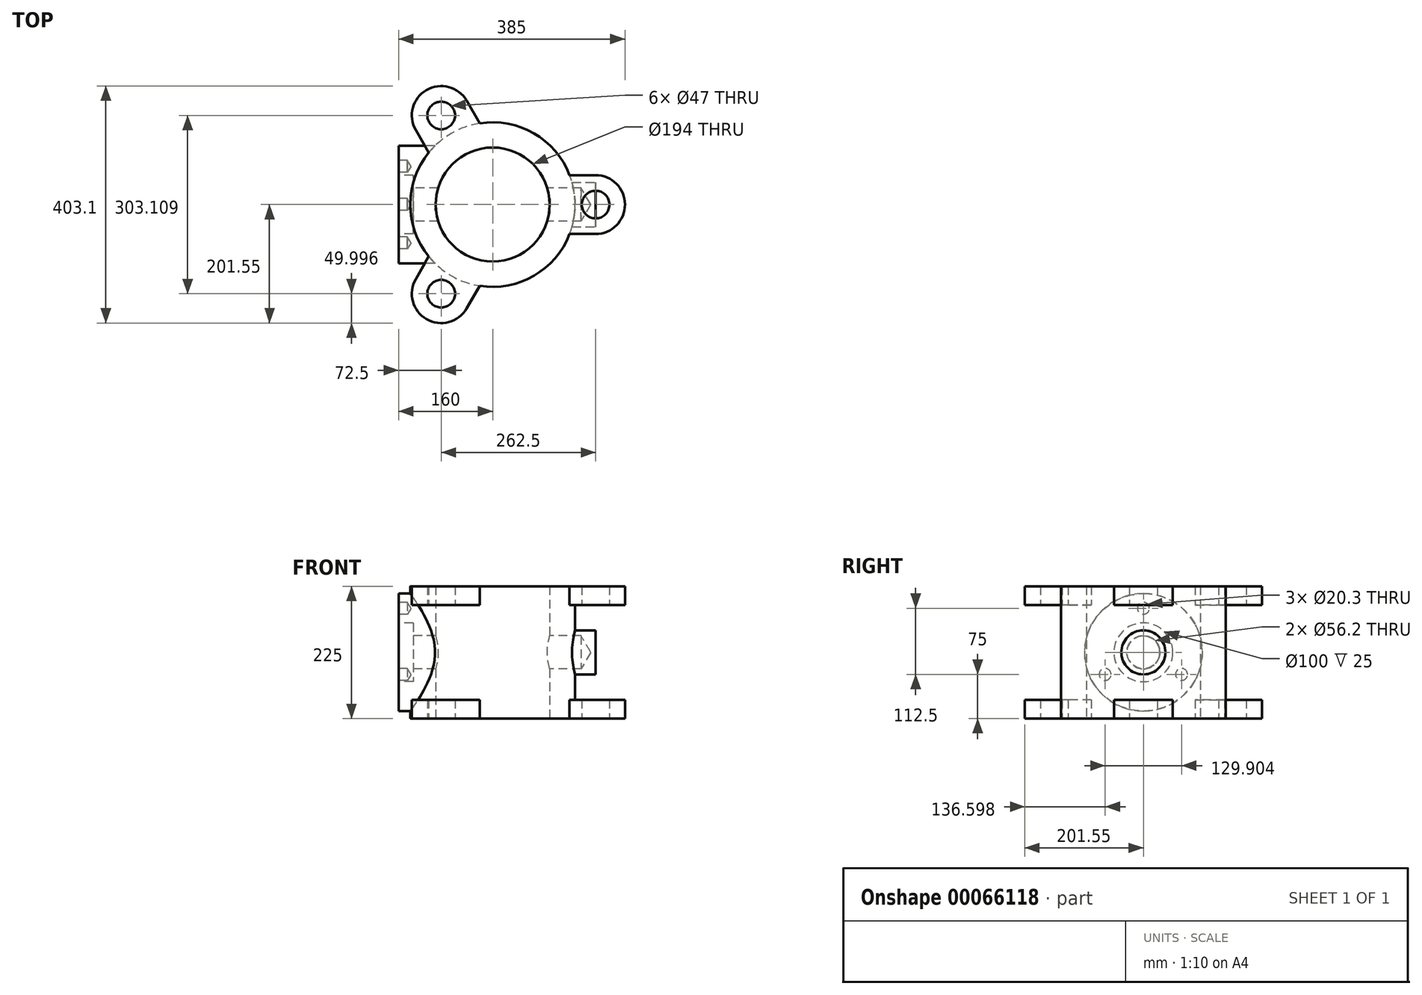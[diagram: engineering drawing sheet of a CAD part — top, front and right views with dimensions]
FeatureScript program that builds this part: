
annotation { "Feature Type Name" : "Feature", "Feature Type Description" : "" }
export const myFeature = defineFeature(function(context is Context, id is Id, definition is map)
    precondition{}
    {
        {
            var Q0;
            Q0=qCreatedBy(makeId("Top.planeOp"),FACE);
            var sketch = newSketch(context, id + "F0", { "sketchPlane" : qUnion([Q0])});
            skArc(sketch, "E0", {"start": v(130.77, 50) * mm, "mid": v(-140, 0) * mm, "end": v(130.77, -50) * mm});
            skCircle(sketch, "E1", {"center": v(0, 0) * mm, "radius": 97 * mm});
            skArc(sketch, "E2", {"start": v(175, -50) * mm, "mid": v(225, 0) * mm, "end": v(175, 50) * mm});
            skCircle(sketch, "E3", {"center": v(175, 0) * mm, "radius": 23.5 * mm});
            skLineSegment(sketch, "E4", {"start": v(130.77, 50) * mm, "end": v(175, 50) * mm});
            skLineSegment(sketch, "E5", {"start": v(130.77, -50) * mm, "end": v(175, -50) * mm});
            skSolve(sketch);
        }
        {
            var Q0;
            Q0=makeQuery(id+"F0.imprint","IMPRINT",FACE,{"disambiguationData":[TD([[makeQuery(id+"F0.imprint","IMPRINT",EDGE,{"derivedFrom":sQuery(id+"F0.wireOp",EDGE,"E0")}),1.0]])]});
            extrude(context, id + "F1", {"entities" : qUnion([Q0]), "depth" : 32 * mm});
        }
        {
            var Q0;
            Q0=makeQuery(id+"F1.opExtrude","SWEPT_BODY",BODY,{"disambiguationData":[OSD([sQuery(id+"F0.wireOp",EDGE,"E0"),sQuery(id+"F0.wireOp",EDGE,"E1"),sQuery(id+"F0.wireOp",EDGE,"E2"),sQuery(id+"F0.wireOp",EDGE,"E3"),sQuery(id+"F0.wireOp",EDGE,"E4"),sQuery(id+"F0.wireOp",EDGE,"E5")])]});
            var Q1;
            Q1=makeQuery(id+"F1.opExtrude","CAP_EDGE",EDGE,{"disambiguationData":[OSD([sQuery(id+"F0.wireOp",EDGE,"E1")])],"isStart":false});
            circularPattern(context, id + "F2", {"operationType" : NewBodyOperationType.ADD, "entities" : qUnion([Q0]), "axis" : qUnion([Q1]), "angle" : 120 * degree, "instanceCount" : 3});
        }
        {
            var Q0;
            {var subQ0=makeQuery(id+"F1.opExtrude","CAP_FACE",FACE,{"disambiguationData":[OSD([sQuery(id+"F0.wireOp",EDGE,"E0"),sQuery(id+"F0.wireOp",EDGE,"E1"),sQuery(id+"F0.wireOp",EDGE,"E2"),sQuery(id+"F0.wireOp",EDGE,"E3"),sQuery(id+"F0.wireOp",EDGE,"E4"),sQuery(id+"F0.wireOp",EDGE,"E5")])],"isStart":false});Q0=makeQuery(id+"F2.boolean.opBoolean","MERGE",FACE,{"derivedFrom":[subQ0,makeQuery(id+"F2.opPattern","COPY",FACE,{"derivedFrom":subQ0,"instanceName":"1"}),makeQuery(id+"F2.opPattern","COPY",FACE,{"derivedFrom":subQ0,"instanceName":"2"})]});}
            var sketch = newSketch(context, id + "F3", { "sketchPlane" : qUnion([Q0])});
            skCircle(sketch, "E6.0", {"center": v(0, 0) * mm, "radius": 97 * mm});
            skCircle(sketch, "E7", {"center": v(0, 0) * mm, "radius": 140 * mm});
            skSolve(sketch);
        }
        {
            var Q0;
            Q0=makeQuery(id+"F3.imprint","IMPRINT",FACE,{"disambiguationData":[TD([[makeQuery(id+"F3.imprint","IMPRINT",EDGE,{"derivedFrom":sQuery(id+"F3.wireOp",EDGE,"E6.0")}),-1.0]])]});
            extrude(context, id + "F4", {"entities" : qUnion([Q0]), "operationType" : NewBodyOperationType.ADD, "depth" : (225 - 64) * mm});
        }
        {
            var Q0;
            Q0=makeQuery(id+"F4.opExtrude","CAP_FACE",FACE,{"disambiguationData":[OSD([sQuery(id+"F3.wireOp",EDGE,"E6.0"),sQuery(id+"F3.wireOp",EDGE,"E7")])],"isStart":false});
            var sketch = newSketch(context, id + "F5", { "sketchPlane" : qUnion([Q0])});
            skLineSegment(sketch, "E8.0.0", {"start": v(175, -50) * mm, "end": v(130.77, -50) * mm});
            skArc(sketch, "E8.0.1", {"start": v(130.77, -50) * mm, "mid": v(70, -121.24) * mm, "end": v(-22.08, -138.25) * mm});
            skLineSegment(sketch, "E8.0.2", {"start": v(-22.08, -138.25) * mm, "end": v(-44.2, -176.55) * mm});
            skArc(sketch, "E8.0.3", {"start": v(-44.2, -176.55) * mm, "mid": v(-112.5, -194.86) * mm, "end": v(-130.8, -126.55) * mm});
            skLineSegment(sketch, "E8.0.4", {"start": v(-130.8, -126.55) * mm, "end": v(-108.68, -88.25) * mm});
            skArc(sketch, "E8.0.5", {"start": v(-108.68, -88.25) * mm, "mid": v(-140, 0) * mm, "end": v(-108.68, 88.25) * mm});
            skLineSegment(sketch, "E8.0.6", {"start": v(-108.68, 88.25) * mm, "end": v(-130.8, 126.55) * mm});
            skArc(sketch, "E8.0.7", {"start": v(-130.8, 126.55) * mm, "mid": v(-112.5, 194.86) * mm, "end": v(-44.2, 176.55) * mm});
            skLineSegment(sketch, "E8.0.8", {"start": v(-44.2, 176.55) * mm, "end": v(-22.08, 138.25) * mm});
            skArc(sketch, "E8.0.9", {"start": v(-22.08, 138.25) * mm, "mid": v(70, 121.24) * mm, "end": v(130.77, 50) * mm});
            skLineSegment(sketch, "E8.0.10", {"start": v(130.77, 50) * mm, "end": v(175, 50) * mm});
            skArc(sketch, "E8.0.11", {"start": v(175, 50) * mm, "mid": v(225, 0) * mm, "end": v(175, -50) * mm});
            skCircle(sketch, "E9.0", {"center": v(-87.5, -151.55) * mm, "radius": 23.5 * mm});
            skCircle(sketch, "E10.0", {"center": v(175, 0) * mm, "radius": 23.5 * mm});
            skCircle(sketch, "E11.0", {"center": v(-87.5, 151.55) * mm, "radius": 23.5 * mm});
            skCircle(sketch, "E12.0", {"center": v(0, 0) * mm, "radius": 97 * mm});
            skSolve(sketch);
        }
        {
            var Q0;
            Q0 = qSketchRegion(id + "F5", true);
            extrude(context, id + "F6", {"entities" : qUnion([Q0]), "operationType" : NewBodyOperationType.ADD, "depth" : 32 * mm});
        }
        {
            var Q0;
            Q0=qCreatedBy(makeId("Right.planeOp"),FACE);
            cPlane(context, id + "F7", {"entities" : qUnion([Q0]), "cplaneType" : CPlaneType.OFFSET, "offset" : 160 * mm, "oppositeDirection" : true, "width" : 150 * mm, "height" : 150 * mm});
        }
        {
            var Q0;
            Q0=qCreatedBy(id+"F7.planeOp",FACE);
            var sketch = newSketch(context, id + "F8", { "sketchPlane" : qUnion([Q0])});
            skCircle(sketch, "E13", {"center": v(0, 112.5) * mm, "radius": 100 * mm});
            skSolve(sketch);
        }
        {
            var Q0;
            Q0=makeQuery(id+"F8.imprint","IMPRINT",FACE,{"disambiguationData":[TD([[makeQuery(id+"F8.imprint","IMPRINT",EDGE,{"derivedFrom":sQuery(id+"F8.wireOp",EDGE,"E13")}),1.0]])]});
            extrude(context, id + "F9", {"entities" : qUnion([Q0]), "operationType" : NewBodyOperationType.ADD, "endBound" : BoundingType.UP_TO_NEXT, "depth" : 25 * mm});
        }
        {
            var Q0;
            Q0=makeQuery(id+"F9.opExtrude","CAP_FACE",FACE,{"disambiguationData":[OSD([sQuery(id+"F8.wireOp",EDGE,"E13")])],"isStart":true});
            var sketch = newSketch(context, id + "F10", { "sketchPlane" : qUnion([Q0])});
            skPoint(sketch, "E14", {"position": v(0, 112.5) * mm});
            skSolve(sketch);
        }
        {
            var Q0;
            Q0=makeQuery(id+"F9.opExtrude","CAP_FACE",FACE,{"disambiguationData":[OSD([sQuery(id+"F8.wireOp",EDGE,"E13")])],"isStart":true});
            var sketch = newSketch(context, id + "F11", { "sketchPlane" : qUnion([Q0])});
            skPoint(sketch, "E15", {"position": v(0, 187.5) * mm});
            skCircle(sketch, "E16", {"center": v(0, 112.5) * mm, "radius": 75 * mm, "construction": true});
            skPoint(sketch, "E17.1.0", {"position": v(-64.95, 75) * mm});
            skPoint(sketch, "E17.2.0", {"position": v(64.95, 75) * mm});
            skSolve(sketch);
        }
        {
            var Q0;
            Q0=sQuery(id+"F11.wireOp",VERTEX,"E15");
            var Q1;
            Q1=sQuery(id+"F11.wireOp",VERTEX,"E17.1.0");
            var Q2;
            Q2=sQuery(id+"F11.wireOp",VERTEX,"E17.2.0");
            var Q3;
            Q3=makeQuery(id+"F1.opExtrude","SWEPT_BODY",BODY,{"disambiguationData":[OSD([sQuery(id+"F0.wireOp",EDGE,"E0"),sQuery(id+"F0.wireOp",EDGE,"E1"),sQuery(id+"F0.wireOp",EDGE,"E2"),sQuery(id+"F0.wireOp",EDGE,"E3"),sQuery(id+"F0.wireOp",EDGE,"E4"),sQuery(id+"F0.wireOp",EDGE,"E5")])]});
            hole(context, id + "F12", {"style" : HoleStyle.SIMPLE, "holeDiameter" : 20.3 * mm, "endStyle" : HoleEndStyle.BLIND, "holeDepth" : 15 * mm, "locations" : qUnion([Q0, Q1, Q2]), "scope" : qUnion([Q3])});
        }
        {
            var Q0;
            Q0=qCreatedBy(makeId("Right.planeOp"),FACE);
            cPlane(context, id + "F13", {"entities" : qUnion([Q0]), "cplaneType" : CPlaneType.OFFSET, "offset" : 175 * mm, "width" : 150 * mm, "height" : 150 * mm});
        }
        {
            var Q0;
            Q0=qCreatedBy(id+"F13.planeOp",FACE);
            var sketch = newSketch(context, id + "F14", { "sketchPlane" : qUnion([Q0])});
            skCircle(sketch, "E18", {"center": v(0, 112.5) * mm, "radius": 37.5 * mm});
            skSolve(sketch);
        }
        {
            var Q0;
            Q0 = qSketchRegion(id + "F14", true);
            var Q1;
            {var subQ0=sQuery(id+"F0.wireOp",EDGE,"E5");var subQ1=sQuery(id+"F0.wireOp",EDGE,"E4");var subQ5=sQuery(id+"F0.wireOp",EDGE,"E0");var subQ11=makeQuery(id+"F1.opExtrude","SWEPT_FACE",FACE,{"disambiguationData":[OSD([subQ1])]});var subQ13=makeQuery(id+"F1.opExtrude","SWEPT_FACE",FACE,{"disambiguationData":[OSD([subQ0])]});var subQ14=makeQuery(id+"F1.opExtrude","SWEPT_FACE",FACE,{"disambiguationData":[OSD([subQ5])]});Q1=makeQuery(id+"F6.boolean.opBoolean","MERGE",FACE,{"derivedFrom":[makeQuery(id+"F4.boolean.opBoolean","MERGE",FACE,{"derivedFrom":[makeQuery(id+"F2.boolean.opBoolean","SPLIT",FACE,{"disambiguationData":[TD([subQ11])],"derivedFrom":subQ14}),makeQuery(id+"F2.boolean.opBoolean","SPLIT",FACE,{"disambiguationData":[TD([subQ13])],"derivedFrom":subQ14}),makeQuery(id+"F2.boolean.opBoolean","SPLIT",FACE,{"disambiguationData":[TD([makeQuery(id+"F2.opPattern","COPY",FACE,{"derivedFrom":subQ11,"instanceName":"1"})])],"derivedFrom":subQ14}),makeQuery(id+"F4.opExtrude","SWEPT_FACE",FACE,{"disambiguationData":[OSD([sQuery(id+"F3.wireOp",EDGE,"E7")])]})]}),makeQuery(id+"F6.opExtrude","SWEPT_FACE",FACE,{"disambiguationData":[OSD([sQuery(id+"F5.wireOp",EDGE,"E8.0.1")])]}),makeQuery(id+"F6.opExtrude","SWEPT_FACE",FACE,{"disambiguationData":[OSD([sQuery(id+"F5.wireOp",EDGE,"E8.0.5")])]}),makeQuery(id+"F6.opExtrude","SWEPT_FACE",FACE,{"disambiguationData":[OSD([sQuery(id+"F5.wireOp",EDGE,"E8.0.9")])]})]});}
            var Q2;
            Q2=makeQuery(id+"F1.opExtrude","SWEPT_BODY",BODY,{"disambiguationData":[OSD([sQuery(id+"F0.wireOp",EDGE,"E0"),sQuery(id+"F0.wireOp",EDGE,"E1"),sQuery(id+"F0.wireOp",EDGE,"E2"),sQuery(id+"F0.wireOp",EDGE,"E3"),sQuery(id+"F0.wireOp",EDGE,"E4"),sQuery(id+"F0.wireOp",EDGE,"E5")])]});
            extrude(context, id + "F15", {"entities" : qUnion([Q0]), "operationType" : NewBodyOperationType.ADD, "endBound" : BoundingType.UP_TO_SURFACE, "oppositeDirection" : true, "endBoundEntityFace" : qUnion([Q1]), "endBoundEntityBody" : qUnion([Q2]), "depth" : 25 * mm});
        }
        {
            var Q0;
            Q0=sQuery(id+"F10.wireOp",VERTEX,"E14");
            var Q1;
            Q1=makeQuery(id+"F1.opExtrude","SWEPT_BODY",BODY,{"disambiguationData":[OSD([sQuery(id+"F0.wireOp",EDGE,"E0"),sQuery(id+"F0.wireOp",EDGE,"E1"),sQuery(id+"F0.wireOp",EDGE,"E2"),sQuery(id+"F0.wireOp",EDGE,"E3"),sQuery(id+"F0.wireOp",EDGE,"E4"),sQuery(id+"F0.wireOp",EDGE,"E5")])]});
            hole(context, id + "F16", {"style" : HoleStyle.C_BORE, "holeDiameter" : 56.2 * mm, "cBoreDiameter" : 100 * mm, "cBoreDepth" : 25 * mm, "endStyle" : HoleEndStyle.BLIND, "holeDepth" : 310 * mm, "locations" : qUnion([Q0]), "scope" : qUnion([Q1])});
        }
    });
